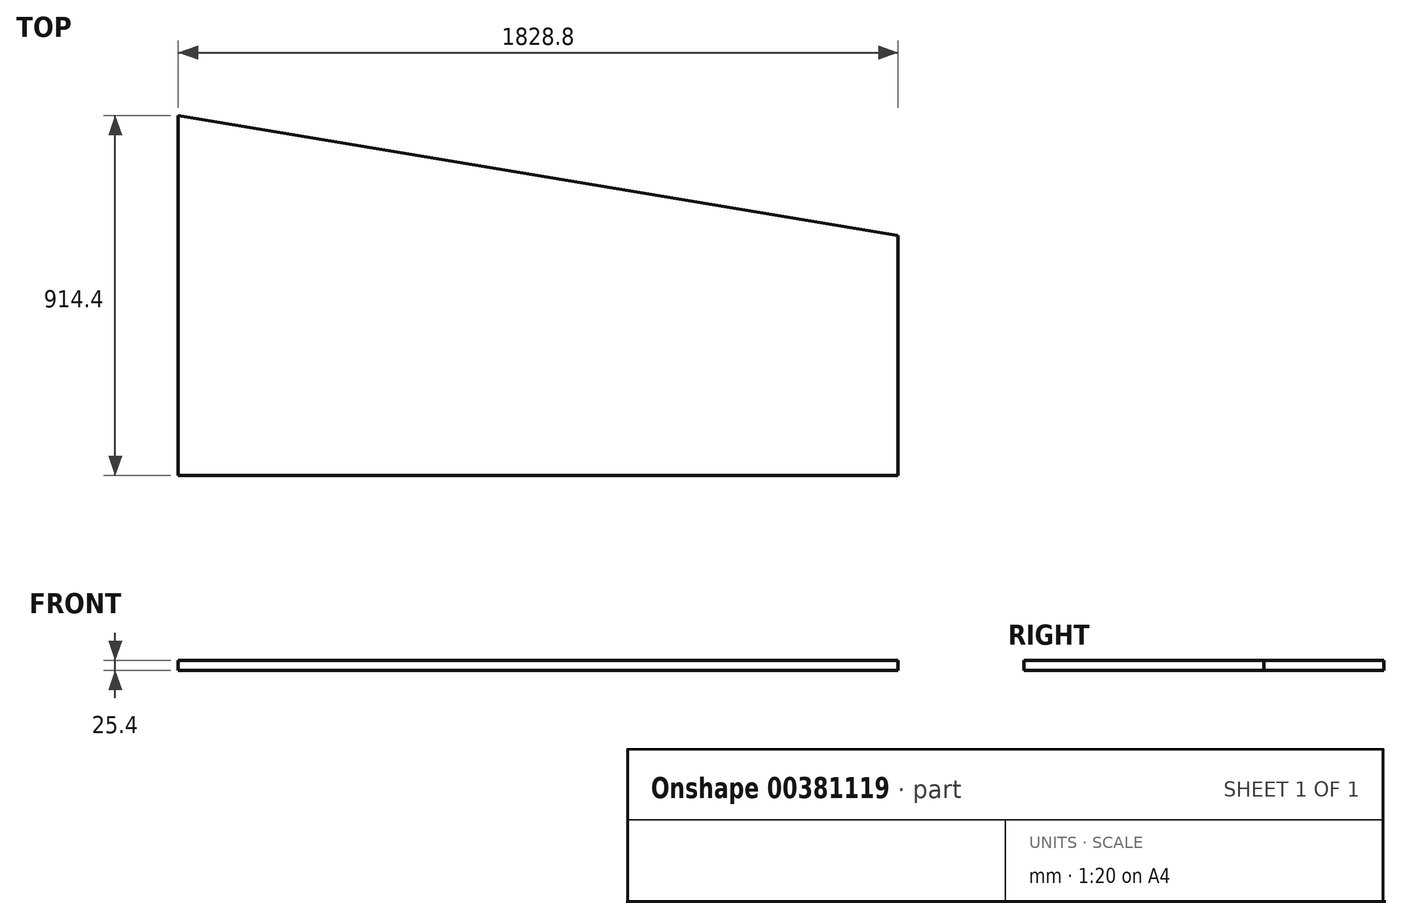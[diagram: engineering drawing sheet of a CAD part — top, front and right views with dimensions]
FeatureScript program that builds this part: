
annotation { "Feature Type Name" : "Feature", "Feature Type Description" : "" }
export const myFeature = defineFeature(function(context is Context, id is Id, definition is map)
    precondition{}
    {
        {
            var Q0;
            Q0=qCreatedBy(makeId("Top.planeOp"),FACE);
            var sketch = newSketch(context, id + "F0", { "sketchPlane" : qUnion([Q0])});
            skSolve(sketch);
        }
        {
            var Q0;
            Q0=qCreatedBy(makeId("Top.planeOp"),FACE);
            var sketch = newSketch(context, id + "F1", { "sketchPlane" : qUnion([Q0])});
            skLineSegment(sketch, "E0", {"start": v(-931.25, -130.48) * mm, "end": v(897.55, -130.48) * mm});
            skLineSegment(sketch, "E1", {"start": v(-931.25, -130.48) * mm, "end": v(-931.25, 783.92) * mm});
            skLineSegment(sketch, "E2", {"start": v(897.55, -130.48) * mm, "end": v(897.55, 479.12) * mm});
            skLineSegment(sketch, "E3", {"start": v(-931.25, 783.92) * mm, "end": v(897.55, 479.12) * mm});
            skSolve(sketch);
        }
        {
            var Q0;
            Q0 = qSketchRegion(id + "F0", true);
            var Q1;
            Q1=makeQuery(id+"F1.imprint","IMPRINT",FACE,{"disambiguationData":[TD([[makeQuery(id+"F1.imprint","IMPRINT",EDGE,{"derivedFrom":sQuery(id+"F1.wireOp",EDGE,"E0")}),1.0]])]});
            extrude(context, id + "F2", {"entities" : qUnion([Q0, Q1]), "depth" : 25.4 * mm});
        }
    });
